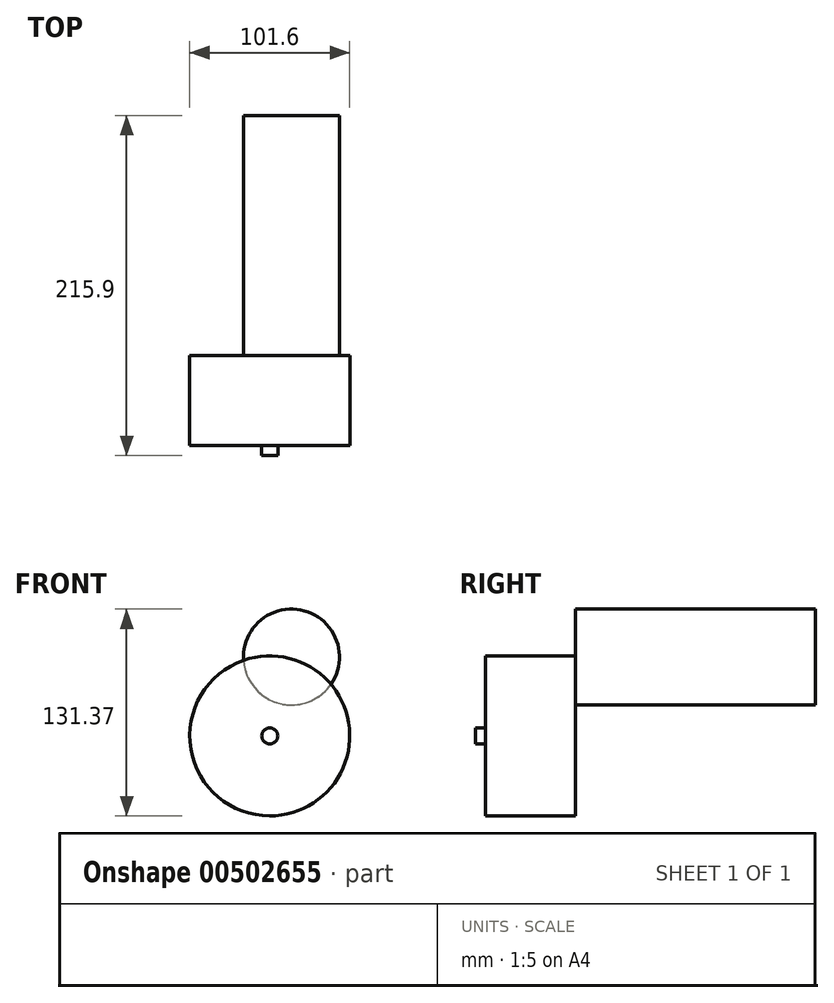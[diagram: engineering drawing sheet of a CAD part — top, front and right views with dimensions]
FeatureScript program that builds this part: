
annotation { "Feature Type Name" : "Feature", "Feature Type Description" : "" }
export const myFeature = defineFeature(function(context is Context, id is Id, definition is map)
    precondition{}
    {
        {
            var Q0;
            Q0=qCreatedBy(makeId("Front.planeOp"),FACE);
            var sketch = newSketch(context, id + "F0", { "sketchPlane" : qUnion([Q0])});
            skCircle(sketch, "E0", {"center": v(-64.76, 60.44) * mm, "radius": 50.8 * mm});
            skSolve(sketch);
        }
        {
            var Q0;
            Q0=qSketchRegion(id+"F0",true);
            extrude(context, id + "F1", {"entities" : qUnion([Q0]), "depth" : 57.15 * mm});
        }
        {
            var Q0;
            Q0=qCreatedBy(makeId("Front.planeOp"),FACE);
            var sketch = newSketch(context, id + "F2", { "sketchPlane" : qUnion([Q0])});
            skCircle(sketch, "E1", {"center": v(-50.97, 110.53) * mm, "radius": 30.48 * mm});
            skSolve(sketch);
        }
        {
            var Q0;
            Q0=qSketchRegion(id+"F2",true);
            extrude(context, id + "F3", {"entities" : qUnion([Q0]), "operationType" : NewBodyOperationType.ADD, "oppositeDirection" : true, "depth" : 152.4 * mm});
        }
        {
            var Q0;
            Q0=makeQuery(id+"F1.opExtrude","CAP_FACE",FACE,{"disambiguationData":[OSD([sQuery(id+"F0.wireOp",EDGE,"E0")])],"isStart":false});
            var sketch = newSketch(context, id + "F4", { "sketchPlane" : qUnion([Q0])});
            skCircle(sketch, "E2", {"center": v(-64.76, 60.44) * mm, "radius": 5.1 * mm});
            skSolve(sketch);
        }
        {
            var Q0;
            Q0=makeQuery(id+"F4.imprint","IMPRINT",FACE,{"disambiguationData":[TD([[makeQuery(id+"F4.imprint","IMPRINT",EDGE,{"derivedFrom":sQuery(id+"F4.wireOp",EDGE,"E2")}),1.0]])]});
            extrude(context, id + "F5", {"entities" : qUnion([Q0]), "depth" : 6.35 * mm});
        }
    });
